# Revit family: BuroSeating_Konfurb Hady Wood Base
name_source: partatom
category: Furniture
units: mm (PartAtom-declared; Revit-internal decimal feet)

## family parameters
Always vertical = Yes
Cut with Voids When Loaded = No
OmniClass Number = 23.40.70.14.64.11
OmniClass Title = Office Furniture
Room Calculation Point = No
Shared = No
Work Plane-Based = No

## types (2) — shared parameters
Assembly Code = E2020
BaseOffset = 18 mm  [stored 0.0590551 ft]
FeetMaterial = BuroSeating_Wood_Yellow Pine
Manufacturer = Buro Seating
NominalDepth = 615 mm  [stored 2.01772 ft]
NominalHeight = 845 mm  [stored 2.77231 ft]
NominalWidth = 600 mm
ProductGroup = Konfurb Hady
ProductPageURL AU = https://buroseating.com
ProductPageURL NZ = https://buroseating.co.nz
ProductRange = Konfurb
SeatHeight = 455 mm  [stored 1.49278 ft]
URL = https://buroseating.co.nz
URL AU = https://buroseating.com
WarrantyDescription = Full 5 year guarantee (excluding upholstery)
zero-valued in all types: Default Elevation

## per-type parameters (varying)
| type | Description |
| KON503-WD-122 | "Konfurb Hady 4 Leg Wood Base (Keylargo, Ash) |
| KON503-WD | "Konfurb Hady 4 Leg Wood Base (Custom) |

note: column(s) folded — value = type name in every type: Model

note: [stored X ft] marks values corroborated as IEEE doubles in the binary element streams (Revit-internal decimal feet)

## geometry (parser evidence)
native form markers: Sweep x5
no freeform markers — native parametric forms only
